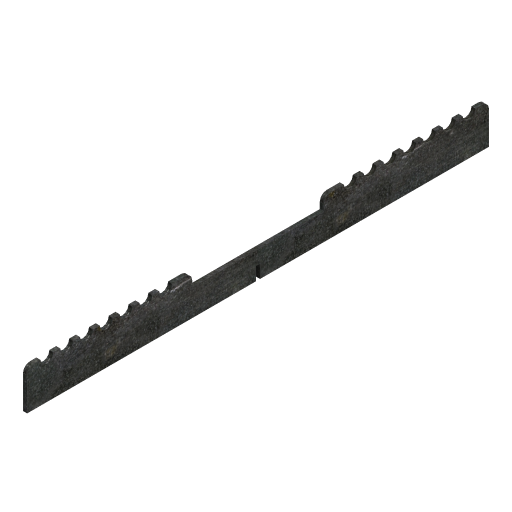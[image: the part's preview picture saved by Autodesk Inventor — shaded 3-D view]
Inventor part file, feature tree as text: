
AUTODESK INVENTOR PART (.ipt)
format: ipt  version: 2024.3 (Build 283343000, 343)  size: 223,744 bytes
history: native  units: mm
features: extrude x3, sketch x3, fillet x2, mirror x1, projected_geometry x1
ambient origin geometry x8: Origin, YZ Plane, XZ Plane, XY Plane, X Axis, Y Axis, Z Axis, Center Point
bodies: Solid1 (feature_tree)
feature tree (10):
  extrude  "Extrusion1"  Depth=350.0mm
  extrude  "Extrusion2"  Depth=100.0mm
  extrude  "Extrusion3"  Depth=10.0mm
  fillet  "Fillet1"  Radius=3.0mm
  fillet  "Fillet2"  Radius=3.1mm
  mirror  "Mirror1"
  sketch  "Sketch1"  dims[d0=30.0mm d1=350.0mm]
  sketch  "Sketch2"  dims[d2=0.0mm d3=100.0mm]
  projected_geometry  "Projected Loop1"
  sketch  "Sketch3"  dims[d4=0.0mm d5=10.0mm d6=3.0mm d7=0.0mm d8=3.1mm d9=20.0mm d10=3.0mm d11=0.0mm d12=10.0mm d13=10.0mm d14=10.0mm d16=10.0mm d17=10.0mm d18=10.0mm d19=15.0mm d20=15.0mm d21=15.0mm d22=15.0mm d23=15.0mm d24=15.0mm d25=10.0mm d26=15.0mm d27=3.0mm d28=0.0mm d29=5.0mm d30=5.0mm]
